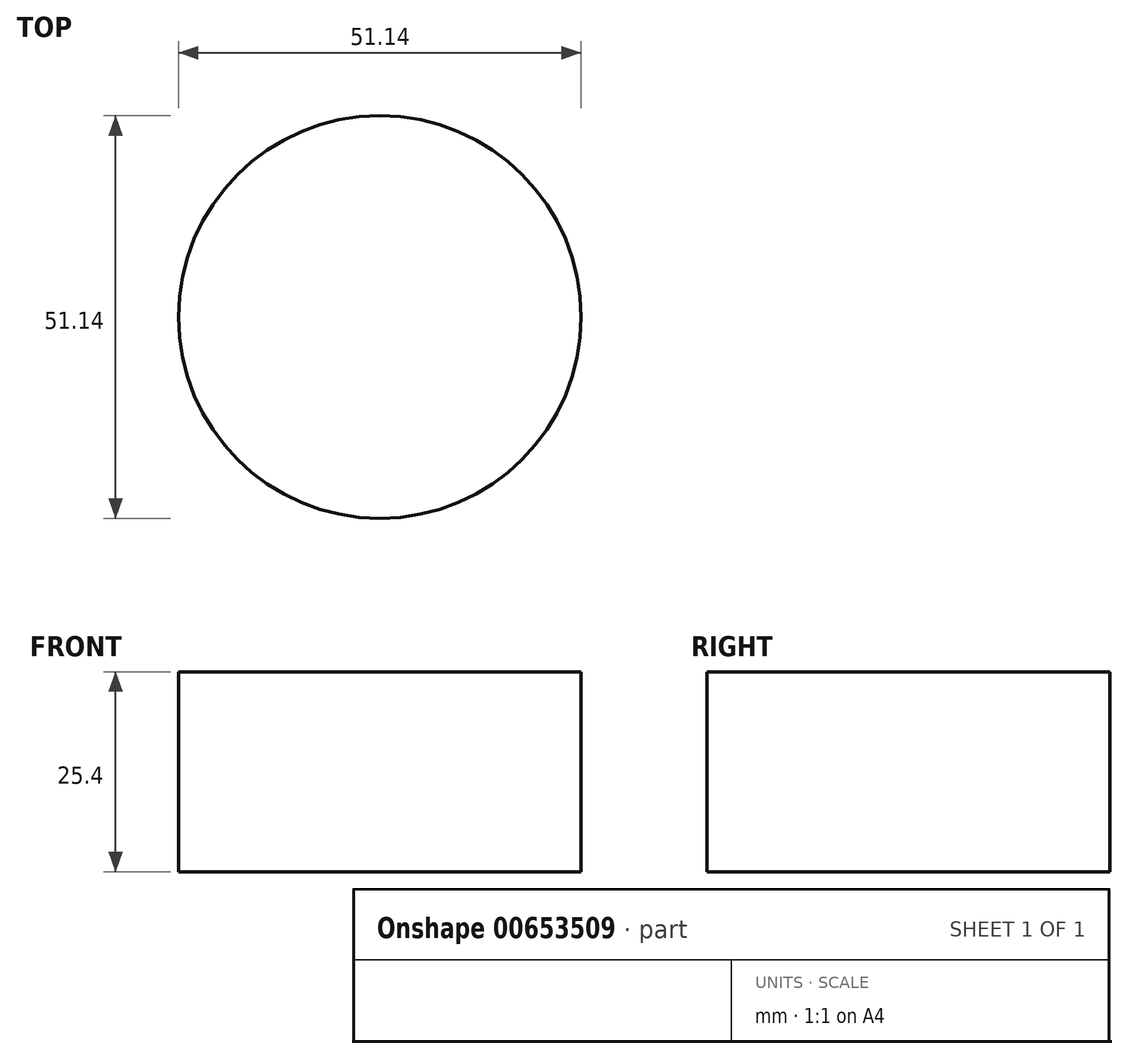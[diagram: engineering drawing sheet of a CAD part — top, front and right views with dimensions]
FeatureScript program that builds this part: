
annotation { "Feature Type Name" : "Feature", "Feature Type Description" : "" }
export const myFeature = defineFeature(function(context is Context, id is Id, definition is map)
    precondition{}
    {
        {
            var Q0;
            Q0=qCreatedBy(makeId("Top.planeOp"),FACE);
            var sketch = newSketch(context, id + "F0", { "sketchPlane" : qUnion([Q0])});
            skCircle(sketch, "E0", {"center": v(0, 0) * mm, "radius": 25.57 * mm});
            skSolve(sketch);
        }
        {
            var Q0;
            Q0 = qSketchRegion(id + "F0", true);
            extrude(context, id + "F1", {"entities" : qUnion([Q0]), "depth" : 25.4 * mm, "offsetDistance" : 25.4 * mm});
        }
    });
